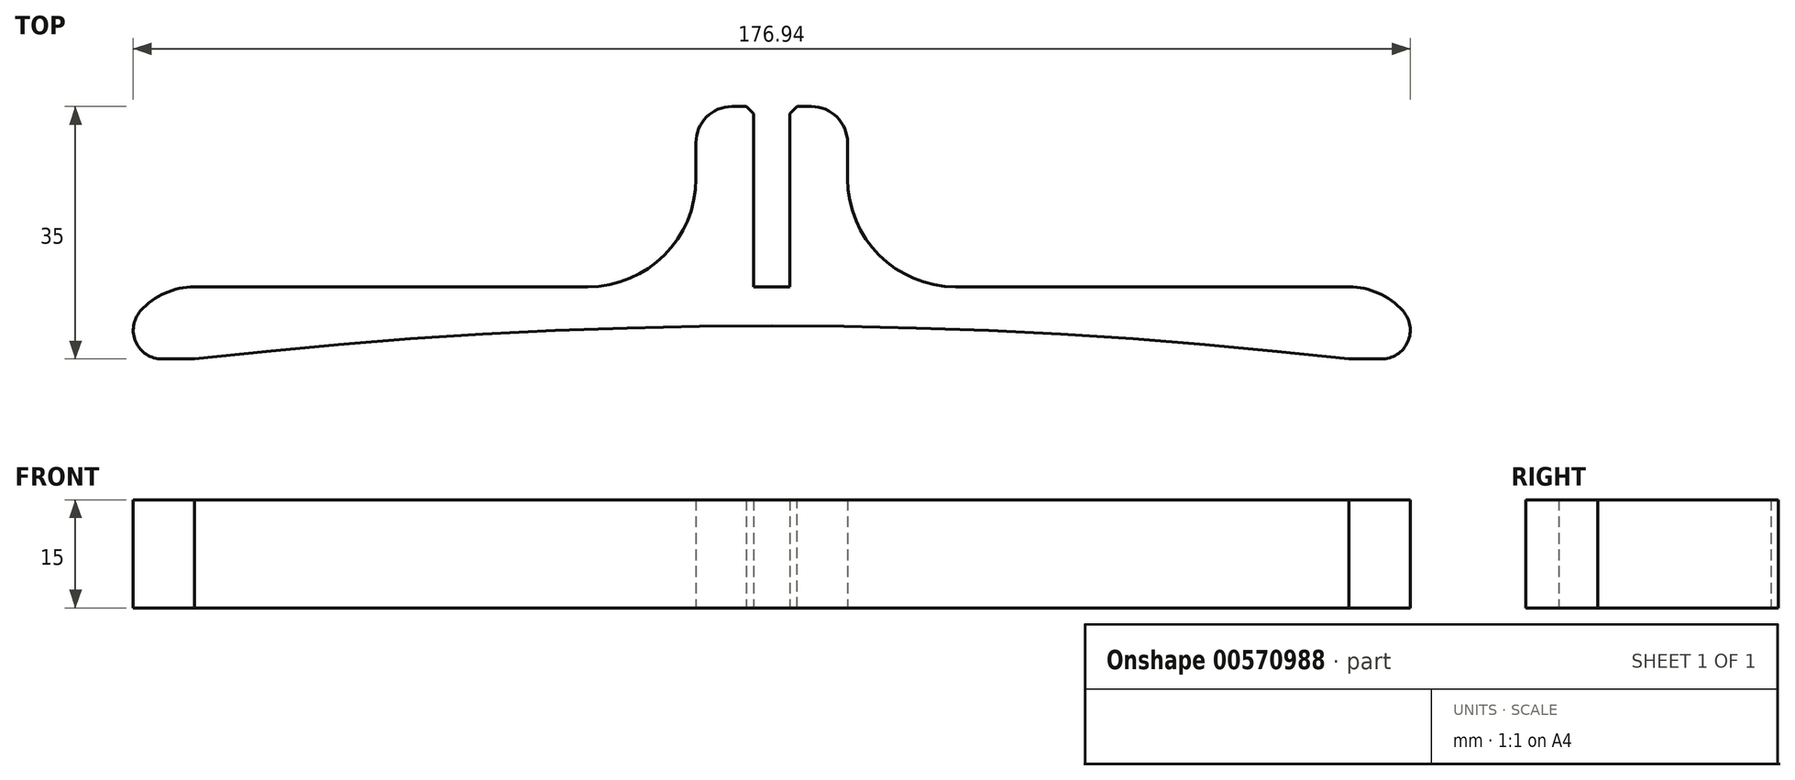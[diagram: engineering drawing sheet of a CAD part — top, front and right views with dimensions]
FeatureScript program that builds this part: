
annotation { "Feature Type Name" : "Feature", "Feature Type Description" : "" }
export const myFeature = defineFeature(function(context is Context, id is Id, definition is map)
    precondition{}
    {
        {
            var Q0;
            Q0=qCreatedBy(makeId("Top.planeOp"),FACE);
            var sketch = newSketch(context, id + "F0", { "sketchPlane" : qUnion([Q0])});
            skLineSegment(sketch, "E0", {"start": v(0, 0) * mm, "end": v(0, 10) * mm});
            skLineSegment(sketch, "E1", {"start": v(180, 0) * mm, "end": v(180, 10) * mm});
            skLineSegment(sketch, "E2", {"start": v(0, 10) * mm, "end": v(79.5, 10) * mm});
            skLineSegment(sketch, "E3", {"start": v(79.5, 10) * mm, "end": v(79.5, 35) * mm});
            skLineSegment(sketch, "E4", {"start": v(79.5, 35) * mm, "end": v(87.5, 35) * mm});
            skLineSegment(sketch, "E5", {"start": v(87.5, 35) * mm, "end": v(87.5, 10) * mm});
            skLineSegment(sketch, "E6", {"start": v(87.5, 10) * mm, "end": v(92.5, 10) * mm});
            skLineSegment(sketch, "E7", {"start": v(92.5, 10) * mm, "end": v(92.5, 35) * mm});
            skLineSegment(sketch, "E8", {"start": v(92.5, 35) * mm, "end": v(100.5, 35) * mm});
            skLineSegment(sketch, "E9", {"start": v(100.5, 35) * mm, "end": v(100.5, 10) * mm});
            skLineSegment(sketch, "E10", {"start": v(100.5, 10) * mm, "end": v(180, 10) * mm});
            skLineSegment(sketch, "E11", {"start": v(180, 0) * mm, "end": v(170, 0) * mm});
            skLineSegment(sketch, "E12", {"start": v(0, 0) * mm, "end": v(10, 0) * mm});
            skArc(sketch, "E13", {"start": v(170, 0) * mm, "mid": v(90, 4.59) * mm, "end": v(10, 0) * mm});
            skLineSegment(sketch, "E14", {"start": v(90, -695.41) * mm, "end": v(90, 10) * mm, "construction": true});
            skSolve(sketch);
        }
        {
            var Q0;
            Q0 = qSketchRegion(id + "F0", true);
            extrude(context, id + "F1", {"entities" : qUnion([Q0]), "depth" : 15 * mm, "offsetDistance" : 25 * mm});
        }
        {
            var Q0;
            Q0=makeQuery(id+"F1.opExtrude","SWEPT_EDGE",EDGE,{"disambiguationData":[OSD([sQuery(id+"F0.wireOp",EDGE,"E9"),sQuery(id+"F0.wireOp",EDGE,"E10")])]});
            var Q1;
            Q1=makeQuery(id+"F1.opExtrude","SWEPT_EDGE",EDGE,{"disambiguationData":[OSD([sQuery(id+"F0.wireOp",EDGE,"E2"),sQuery(id+"F0.wireOp",EDGE,"E3")])]});
            fillet(context, id + "F2", {"entities" : qUnion([Q0, Q1]), "radius" : 15 * mm, "tangentPropagation" : true, "allowEdgeOverflow" : false});
        }
        {
            var Q0;
            Q0=makeQuery(id+"F1.opExtrude","SWEPT_EDGE",EDGE,{"disambiguationData":[OSD([sQuery(id+"F0.wireOp",EDGE,"E1"),sQuery(id+"F0.wireOp",EDGE,"E10")])]});
            var Q1;
            Q1=makeQuery(id+"F1.opExtrude","SWEPT_EDGE",EDGE,{"disambiguationData":[OSD([sQuery(id+"F0.wireOp",EDGE,"E0"),sQuery(id+"F0.wireOp",EDGE,"E2")])]});
            fillet(context, id + "F3", {"entities" : qUnion([Q0, Q1]), "radius" : 10 * mm, "tangentPropagation" : true, "allowEdgeOverflow" : false});
        }
        {
            var Q0;
            Q0=makeQuery(id+"F3.opFillet","BLEND_EDGE",EDGE,{"blendedFrom":[makeQuery(id+"F1.opExtrude","SWEPT_EDGE",EDGE,{"disambiguationData":[OSD([sQuery(id+"F0.wireOp",EDGE,"E0"),sQuery(id+"F0.wireOp",EDGE,"E2")])]}),makeQuery(id+"F1.opExtrude","SWEPT_FACE",FACE,{"disambiguationData":[OSD([sQuery(id+"F0.wireOp",EDGE,"E12")])]})],"blendedInto":[makeQuery(id+"F1.opExtrude","SWEPT_FACE",FACE,{"disambiguationData":[OSD([sQuery(id+"F0.wireOp",EDGE,"E12")])]})]});
            var Q1;
            Q1=makeQuery(id+"F3.opFillet","BLEND_EDGE",EDGE,{"blendedFrom":[makeQuery(id+"F1.opExtrude","SWEPT_EDGE",EDGE,{"disambiguationData":[OSD([sQuery(id+"F0.wireOp",EDGE,"E1"),sQuery(id+"F0.wireOp",EDGE,"E10")])]}),makeQuery(id+"F1.opExtrude","SWEPT_FACE",FACE,{"disambiguationData":[OSD([sQuery(id+"F0.wireOp",EDGE,"E11")])]})],"blendedInto":[makeQuery(id+"F1.opExtrude","SWEPT_FACE",FACE,{"disambiguationData":[OSD([sQuery(id+"F0.wireOp",EDGE,"E11")])]})]});
            fillet(context, id + "F4", {"entities" : qUnion([Q0, Q1]), "radius" : 4 * mm, "tangentPropagation" : true, "allowEdgeOverflow" : false});
        }
        {
            var Q0;
            Q0=makeQuery(id+"F1.opExtrude","SWEPT_EDGE",EDGE,{"disambiguationData":[OSD([sQuery(id+"F0.wireOp",EDGE,"E3"),sQuery(id+"F0.wireOp",EDGE,"E4")])]});
            var Q1;
            Q1=makeQuery(id+"F1.opExtrude","SWEPT_EDGE",EDGE,{"disambiguationData":[OSD([sQuery(id+"F0.wireOp",EDGE,"E8"),sQuery(id+"F0.wireOp",EDGE,"E9")])]});
            fillet(context, id + "F5", {"entities" : qUnion([Q0, Q1]), "radius" : 5 * mm, "tangentPropagation" : true, "allowEdgeOverflow" : false});
        }
        {
            var Q0;
            Q0=makeQuery(id+"F1.opExtrude","SWEPT_EDGE",EDGE,{"disambiguationData":[OSD([sQuery(id+"F0.wireOp",EDGE,"E4"),sQuery(id+"F0.wireOp",EDGE,"E5")])]});
            var Q1;
            Q1=makeQuery(id+"F1.opExtrude","SWEPT_EDGE",EDGE,{"disambiguationData":[OSD([sQuery(id+"F0.wireOp",EDGE,"E7"),sQuery(id+"F0.wireOp",EDGE,"E8")])]});
            chamfer(context, id + "F6", {"entities" : qUnion([Q0, Q1]), "width" : 1 * mm, "tangentPropagation" : true});
        }
    });
